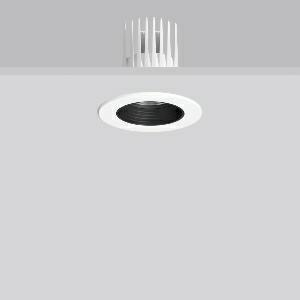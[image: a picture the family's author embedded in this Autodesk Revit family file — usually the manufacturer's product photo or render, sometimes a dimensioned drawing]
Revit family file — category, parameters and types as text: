
# Revit family: heledon_mini_e_901753_002_3_76_cefc
name_source: partatom
category: Lighting Fixtures
units: mm (PartAtom-declared; Revit-internal decimal feet)

## family parameters
Cut with Voids When Loaded = No
Host = Face
Light Source = No
Part Type = Normal
Room Calculation Point = No
Round Connector Dimension = Use Diameter
Shared = No

## types (1)
- HELEDON mini E (1 x LED Modul 935, 2900 lm, 3500)
    Apparent Load = 29 VA
    Approval mark = CE
    CIE Flux Codes = 98 100 100 100 100
    Color Rendering = 92
    Color Temperature = 3500
    Default Elevation = 1800 mm
    Description = Series: HELEDON mini
Round recessed downlight. Housing: die-cast aluminium, powder-coated. Black plastic ring and recessed LED to prevent glare from the side. Optical assembly with lens made of plastic (polycarbonate) for the best homogeneous light distribution - can be changed without tools. Best colour rendering index Ra>90. Suitable for Recessed ceiling mounting. Installation without tools thanks to spring fastening system. Including separate LED converter with connecting cable 600 mm.High quality converter without flickering and stroboscopic effect. Through-wiring box (5 pole) available as accessory. The following accessories can be mounted without use of tools: interchangeable lenses, decorative glasses, honeycomb louvre, clear and frosted diffusers, white interchangeable plastic ring. 
Colour: traffic white, matt (RAL 9016)
Diameter: 124 mm
Height: 3 mm
Cut-out diameter: 114 mm
Recess height: 170 mm
Luminaire: recess height: 120 mm
Lamp: LED
Socket: without socket
Colour temperature: 3500K
Colour rendering index (CRI): 92
System power: 29 W
Rated luminous flux: 2900 lm
Luminous efficiency: 100 lm/W
Control gear: Converter, dimmable, DALI
Protection class: II
Type of protection: IP 20
    Height = 0 mm  [stored 0 ft]
    Lamp = 1 x LED Modul 935
    Lamp Light Flux = 2900 lm
    Lamp count = 1
    Length = 124 mm  [stored 0.406824 ft]
    Lifetime = 50000 h
    Luminous efficacy = 100 lm/W
    Manufacturer = RZB
    ModVariant = No
    Model = 901753.002.3.76
    Mounting Place = Ceiling
    Mounting Type = Recessed
    Number of Poles = 1
    OnlyDefault = Yes
    Power Factor = 1
    Product Name = HELEDON mini E
    Product group = Recessed downlights
    ProductGroupID = 402
    Protection Class = Protection class II
    Protection Degree = IP 20
    RLX_Detail_Level = 1
    RLX_Emergency_Light_Flux = 0 lm
    RLX_Emergency_Type = 0
    RLX_Emergency_Type_DB = No
    RlxData = <blob elided: 128677 chars, md5=cac4258b>
    Socket = socket
    Standby Power = 0 W
    System Light Flux = 2900 lm
    System Power = 29 W
    Type Comments = Product without accessories
    Type Image = 901656.002.jpg
    URL = http://relux.com
    VarID = ---
    Voltage = 230 V
    Voltage Range = 220-240 V
    Weight = 0.00 kg
    Width = 0 mm  [stored 0 ft]

note: [stored X ft] marks values corroborated as IEEE doubles in the binary element streams (Revit-internal decimal feet)

## geometry (parser evidence)
native form markers: Blend x4, Sweep x12
no freeform markers — native parametric forms only
